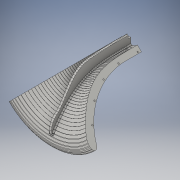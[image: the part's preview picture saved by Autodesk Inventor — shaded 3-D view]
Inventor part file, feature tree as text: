
AUTODESK INVENTOR PART (.ipt)
format: ipt  version: 2016 SP1 (Build 200210100, 210)  size: 3,869,184 bytes
history: native  units: in
note: dims shown in document units (in); Inventor stores cm internally (conversion verified against a paired STEP export)
features: hole x1, sketch x1, other x1
ambient origin geometry x8: Origin, YZ Plane, XZ Plane, XY Plane, X Axis, Y Axis, Z Axis, Center Point
bodies: Solid1 (feature_tree)
feature tree (3):
  hole  "Hole1"  [1 undecoded]
  sketch  "Sketch1"  dims[d0=0.516in d1=0.171in d2=0.432in d3=0.375in d4=0.25in d5=0.5635in d6=0.64in d7=0.8108in]
  parser-record x1  (decoder bookkeeping rows leaked as tree rows — omitted from the tree; the rows remain in map.json)
note: 1 required parameter value undecoded (feature->parameter linkage not recoverable at this tier; creation-order binding heuristic only, values carry confidence <= 0.55)
